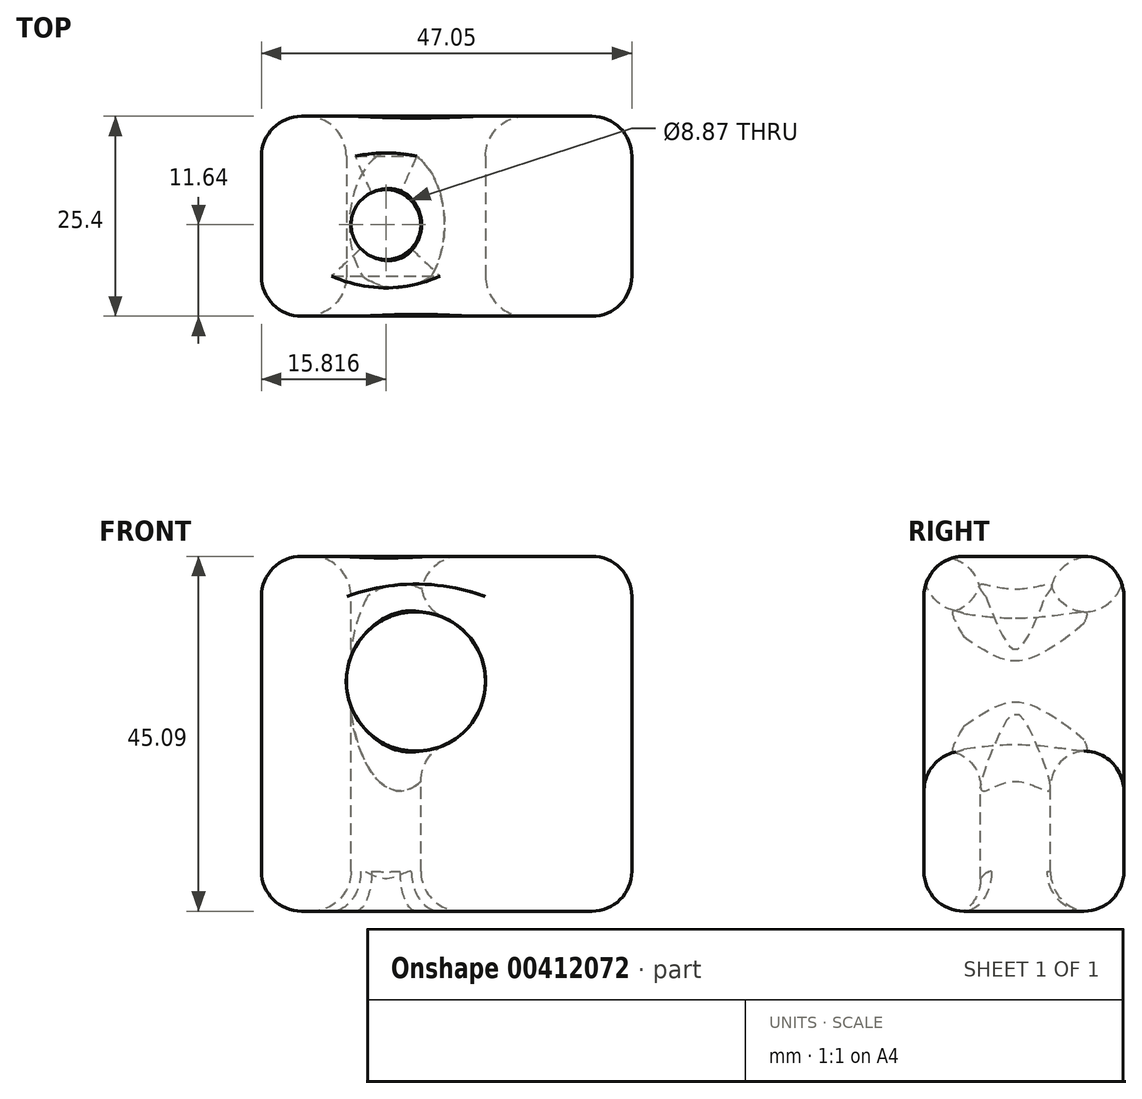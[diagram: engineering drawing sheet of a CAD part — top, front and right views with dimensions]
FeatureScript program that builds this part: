
annotation { "Feature Type Name" : "Feature", "Feature Type Description" : "" }
export const myFeature = defineFeature(function(context is Context, id is Id, definition is map)
    precondition{}
    {
        {
            var Q0;
            Q0=qCreatedBy(makeId("Front.planeOp"),FACE);
            var sketch = newSketch(context, id + "F0", { "sketchPlane" : qUnion([Q0])});
            skLineSegment(sketch, "E0.bottom", {"start": v(-39.58, 19.73) * mm, "end": v(7.47, 19.73) * mm});
            skLineSegment(sketch, "E0.top", {"start": v(-39.58, -25.36) * mm, "end": v(7.47, -25.36) * mm});
            skLineSegment(sketch, "E0.left", {"start": v(-39.58, 19.73) * mm, "end": v(-39.58, -25.36) * mm});
            skLineSegment(sketch, "E0.right", {"start": v(7.47, 19.73) * mm, "end": v(7.47, -25.36) * mm});
            skSolve(sketch);
        }
        {
            var Q0;
            Q0=makeQuery(id+"F0.imprint","IMPRINT",FACE,{"disambiguationData":[TD([[makeQuery(id+"F0.imprint","IMPRINT",EDGE,{"derivedFrom":sQuery(id+"F0.wireOp",EDGE,"E0.bottom")}),-1.0]])]});
            extrude(context, id + "F1", {"entities" : qUnion([Q0]), "depth" : 25.4 * mm});
        }
        {
            var Q0;
            Q0=makeQuery(id+"F1.opExtrude","CAP_FACE",FACE,{"disambiguationData":[OSD([sQuery(id+"F0.wireOp",EDGE,"E0.bottom"),sQuery(id+"F0.wireOp",EDGE,"E0.top"),sQuery(id+"F0.wireOp",EDGE,"E0.left"),sQuery(id+"F0.wireOp",EDGE,"E0.right")])],"isStart":false});
            var sketch = newSketch(context, id + "F2", { "sketchPlane" : qUnion([Q0])});
            skCircle(sketch, "E1", {"center": v(-19.96, 3.83) * mm, "radius": 8.84 * mm});
            skSolve(sketch);
        }
        {
            var Q0;
            Q0=makeQuery(id+"F2.imprint","IMPRINT",FACE,{"disambiguationData":[TD([[makeQuery(id+"F2.imprint","IMPRINT",EDGE,{"derivedFrom":sQuery(id+"F2.wireOp",EDGE,"E1")}),1.0]])]});
            extrude(context, id + "F3", {"entities" : qUnion([Q0]), "operationType" : NewBodyOperationType.REMOVE, "endBound" : BoundingType.THROUGH_ALL, "oppositeDirection" : true, "depth" : 25.4 * mm});
        }
        {
            var Q0;
            Q0=makeQuery(id+"F1.opExtrude","SWEPT_FACE",FACE,{"disambiguationData":[OSD([sQuery(id+"F0.wireOp",EDGE,"E0.bottom")])]});
            var sketch = newSketch(context, id + "F4", { "sketchPlane" : qUnion([Q0])});
            skCircle(sketch, "E2", {"center": v(-23.76, -13.76) * mm, "radius": 4.43 * mm});
            skSolve(sketch);
        }
        {
            var Q0;
            Q0=makeQuery(id+"F4.imprint","IMPRINT",FACE,{"disambiguationData":[TD([[makeQuery(id+"F4.imprint","IMPRINT",EDGE,{"derivedFrom":sQuery(id+"F4.wireOp",EDGE,"E2")}),1.0]])]});
            extrude(context, id + "F5", {"entities" : qUnion([Q0]), "operationType" : NewBodyOperationType.REMOVE, "endBound" : BoundingType.THROUGH_ALL, "oppositeDirection" : true, "depth" : 25.4 * mm});
        }
        {
            var Q0;
            Q0=makeQuery(id+"F1.opExtrude","SWEPT_FACE",FACE,{"disambiguationData":[OSD([sQuery(id+"F0.wireOp",EDGE,"E0.bottom")])]});
            var Q1;
            Q1=makeQuery(id+"F1.opExtrude","SWEPT_FACE",FACE,{"disambiguationData":[OSD([sQuery(id+"F0.wireOp",EDGE,"E0.right")])]});
            var Q2;
            Q2=makeQuery(id+"F1.opExtrude","CAP_FACE",FACE,{"disambiguationData":[OSD([sQuery(id+"F0.wireOp",EDGE,"E0.bottom"),sQuery(id+"F0.wireOp",EDGE,"E0.top"),sQuery(id+"F0.wireOp",EDGE,"E0.left"),sQuery(id+"F0.wireOp",EDGE,"E0.right")])],"isStart":false});
            var Q3;
            Q3=makeQuery(id+"F3.boolean.opBoolean","COPY",FACE,{"derivedFrom":makeQuery(id+"F3.opExtrude","SWEPT_FACE",FACE,{"disambiguationData":[OSD([sQuery(id+"F2.wireOp",EDGE,"E1")])]})});
            var Q4;
            Q4=makeQuery(id+"F1.opExtrude","CAP_FACE",FACE,{"disambiguationData":[OSD([sQuery(id+"F0.wireOp",EDGE,"E0.bottom"),sQuery(id+"F0.wireOp",EDGE,"E0.top"),sQuery(id+"F0.wireOp",EDGE,"E0.left"),sQuery(id+"F0.wireOp",EDGE,"E0.right")])],"isStart":true});
            fillet(context, id + "F6", {"entities" : qUnion([Q0, Q1, Q2, Q3, Q4]), "radius" : 5.08 * mm, "tangentPropagation" : true, "allowEdgeOverflow" : false});
        }
        {
            var Q0;
            Q0=makeQuery(id+"F1.opExtrude","SWEPT_FACE",FACE,{"disambiguationData":[OSD([sQuery(id+"F0.wireOp",EDGE,"E0.top")])]});
            fillet(context, id + "F7", {"entities" : qUnion([Q0]), "radius" : 5.08 * mm, "tangentPropagation" : true, "allowEdgeOverflow" : false});
        }
    });
